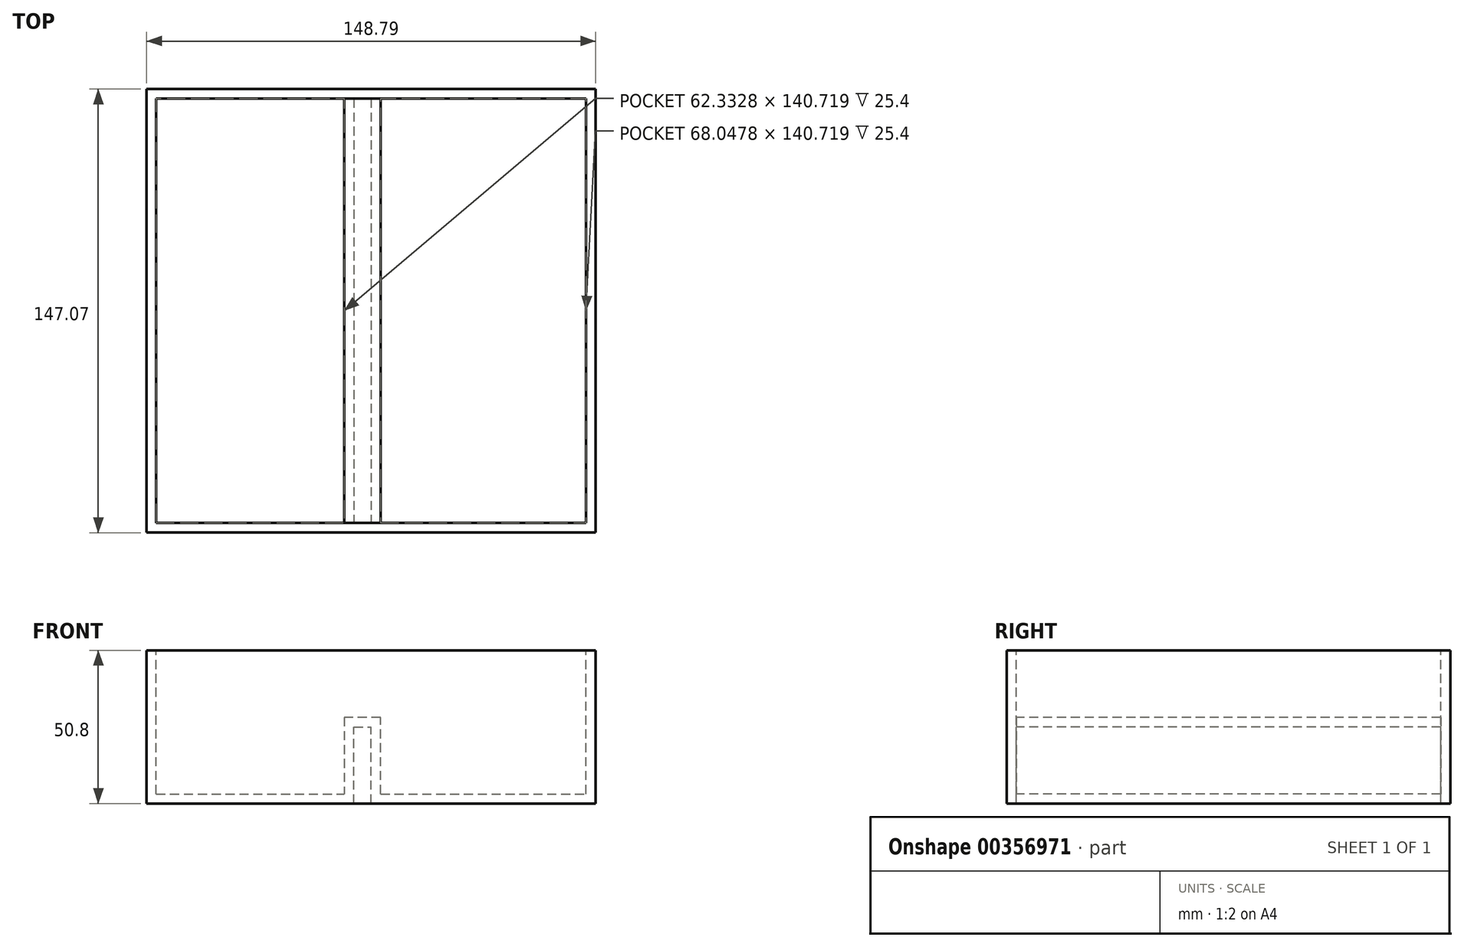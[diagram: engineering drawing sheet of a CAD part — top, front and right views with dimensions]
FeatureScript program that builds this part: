
annotation { "Feature Type Name" : "Feature", "Feature Type Description" : "" }
export const myFeature = defineFeature(function(context is Context, id is Id, definition is map)
    precondition{}
    {
        {
            var Q0;
            Q0=qCreatedBy(makeId("Top.planeOp"),FACE);
            var sketch = newSketch(context, id + "F0", { "sketchPlane" : qUnion([Q0])});
            skLineSegment(sketch, "E0.bottom", {"start": v(-73.4, 71.66) * mm, "end": v(75.4, 71.66) * mm});
            skLineSegment(sketch, "E0.top", {"start": v(-73.4, -75.4) * mm, "end": v(75.4, -75.4) * mm});
            skLineSegment(sketch, "E0.left", {"start": v(-73.4, 71.66) * mm, "end": v(-73.4, -75.4) * mm});
            skLineSegment(sketch, "E0.right", {"start": v(75.4, 71.66) * mm, "end": v(75.4, -75.4) * mm});
            skSolve(sketch);
        }
        {
            var Q0;
            Q0 = qSketchRegion(id + "F0", true);
            extrude(context, id + "F1", {"entities" : qUnion([Q0]), "oppositeDirection" : true, "depth" : 50.8 * mm});
        }
        {
            var Q0;
            Q0=makeQuery(id+"F1.opExtrude","CAP_FACE",FACE,{"disambiguationData":[OSD([sQuery(id+"F0.wireOp",EDGE,"E0.bottom"),sQuery(id+"F0.wireOp",EDGE,"E0.top"),sQuery(id+"F0.wireOp",EDGE,"E0.left"),sQuery(id+"F0.wireOp",EDGE,"E0.right")])],"isStart":true});
            var sketch = newSketch(context, id + "F2", { "sketchPlane" : qUnion([Q0])});
            skLineSegment(sketch, "E1.bottom", {"start": v(-4.72, 68.49) * mm, "end": v(1, 68.49) * mm});
            skLineSegment(sketch, "E1.left", {"start": v(-4.72, 68.49) * mm, "end": v(-4.72, -72.23) * mm});
            skLineSegment(sketch, "E1.right", {"start": v(1, 68.49) * mm, "end": v(1, -72.23) * mm});
            skLineSegment(sketch, "E2", {"start": v(1, -72.23) * mm, "end": v(-4.72, -72.23) * mm});
            skPoint(sketch, "E1.top.end.orphan", {"position": v(1, -75.4) * mm});
            skSolve(sketch);
        }
        {
            var Q0;
            Q0 = qSketchRegion(id + "F2", true);
            extrude(context, id + "F3", {"entities" : qUnion([Q0]), "operationType" : NewBodyOperationType.REMOVE, "oppositeDirection" : true, "depth" : 63.5 * mm, "hasSecondDirection" : true, "secondDirectionOppositeDirection" : true, "secondDirectionDepth" : 25.4 * mm});
        }
        {
            var Q0;
            Q0=makeQuery(id+"F1.opExtrude","CAP_FACE",FACE,{"disambiguationData":[OSD([sQuery(id+"F0.wireOp",EDGE,"E0.bottom"),sQuery(id+"F0.wireOp",EDGE,"E0.top"),sQuery(id+"F0.wireOp",EDGE,"E0.left"),sQuery(id+"F0.wireOp",EDGE,"E0.right")])],"isStart":true});
            shell(context, id + "F4", {"entities" : qUnion([Q0]), "thickness" : 3.17 * mm});
        }
    });
